FCSTD DOCUMENT  (FreeCAD 0.20R0.20)
Label: 009
License: All rights reserved
LicenseURL: http://en.wikipedia.org/wiki/All_rights_reserved
objects: Sketcher::SketchObject×1
note: 1 computed .brp shape members not serialized (recipe doc carries the construction recipe); baked Part::Feature solids carry a one-line shape summary decoded from their .brp

FEATURE [Sketcher::SketchObject] Sketch  label="baseL"
  FullyConstrained = false
  sketch-geometry (38):
    g0: LineSegment StartX=0 StartY=0 StartZ=0 EndX=0 EndY=200 EndZ=0
    g1: LineSegment StartX=390 StartY=200 StartZ=0 EndX=390 EndY=0 EndZ=0
    g2: LineSegment StartX=0 StartY=200 StartZ=0 EndX=190 EndY=200 EndZ=0
    g3: LineSegment StartX=0 StartY=0 StartZ=0 EndX=190 EndY=0 EndZ=0
    g4: LineSegment StartX=390 StartY=200 StartZ=0 EndX=200 EndY=200 EndZ=0
    g5: LineSegment StartX=390 StartY=0 StartZ=0 EndX=200 EndY=0 EndZ=0
    g6: LineSegment StartX=190 StartY=0 StartZ=0 EndX=190 EndY=14 EndZ=0
    g7: LineSegment StartX=200 StartY=0 StartZ=0 EndX=200 EndY=14 EndZ=0
    g8: LineSegment StartX=24 StartY=186 StartZ=0 EndX=190 EndY=105.929 EndZ=0
    g9: LineSegment StartX=16 StartY=178 StartZ=0 EndX=177.707 EndY=100 EndZ=0
    g10: LineSegment StartX=16 StartY=22 StartZ=0 EndX=177.707 EndY=100 EndZ=0
    g11: LineSegment StartX=24 StartY=14 StartZ=0 EndX=190 EndY=94.0706 EndZ=0
    g12: LineSegment StartX=16 StartY=22 StartZ=0 EndX=16 EndY=178 EndZ=0
    g13: LineSegment StartX=212.293 StartY=100 StartZ=0 EndX=374 EndY=22 EndZ=0
    g14: LineSegment StartX=200 StartY=94.0706 StartZ=0 EndX=366 EndY=14 EndZ=0
    g15: LineSegment StartX=374 StartY=178 StartZ=0 EndX=212.293 EndY=100 EndZ=0
    g16: LineSegment StartX=200 StartY=105.929 StartZ=0 EndX=366 EndY=186 EndZ=0
    g17: LineSegment StartX=212.293 StartY=100 StartZ=0 EndX=200 EndY=100 EndZ=0
    g18: LineSegment StartX=374 StartY=178 StartZ=0 EndX=374 EndY=22 EndZ=0
    g19: LineSegment StartX=366 StartY=14 StartZ=0 EndX=200 EndY=14 EndZ=0
    g20: LineSegment StartX=200 StartY=186 StartZ=0 EndX=366 EndY=186 EndZ=0
    g21: LineSegment StartX=24 StartY=14 StartZ=0 EndX=190 EndY=14 EndZ=0
    g22: LineSegment StartX=190 StartY=186 StartZ=0 EndX=24 EndY=186 EndZ=0
    g23: LineSegment StartX=177.707 StartY=100 StartZ=0 EndX=190 EndY=100 EndZ=0
    g24: Circle CenterX=190 CenterY=100 CenterZ=0 NormalX=0 NormalY=0 NormalZ=1 AngleXU=0 Radius=22.2927
    g25: Circle CenterX=190 CenterY=100 CenterZ=0 NormalX=0 NormalY=0 NormalZ=1 AngleXU=0 Radius=11.6257
    g26: LineSegment StartX=190 StartY=94.0706 StartZ=0 EndX=190.36 EndY=94.2444 EndZ=0
    g27: Circle CenterX=200 CenterY=100 CenterZ=0 NormalX=0 NormalY=0 NormalZ=1 AngleXU=0 Radius=11.2273
    g28: Circle CenterX=200 CenterY=100 CenterZ=0 NormalX=0 NormalY=0 NormalZ=1 AngleXU=0 Radius=22.2927
    g29: LineSegment StartX=190 StartY=200 StartZ=0 EndX=190 EndY=195.3 EndZ=0
    g30: LineSegment StartX=200 StartY=200 StartZ=0 EndX=200 EndY=195 EndZ=0
    g31: LineSegment StartX=190 StartY=195.3 StartZ=0 EndX=184 EndY=195.3 EndZ=0
    g32: LineSegment StartX=184 StartY=195.3 StartZ=0 EndX=184 EndY=193 EndZ=0
    g33: LineSegment StartX=184 StartY=193 StartZ=0 EndX=184 EndY=196.5 EndZ=0
    g34: Circle CenterX=184 CenterY=193 CenterZ=0 NormalX=0 NormalY=0 NormalZ=1 AngleXU=0 Radius=3.5
    g35: LineSegment StartX=190 StartY=186 StartZ=0 EndX=190 EndY=190.7 EndZ=0
    g36: LineSegment StartX=190 StartY=190.7 StartZ=0 EndX=184.163 EndY=190.7 EndZ=0
    g37: LineSegment StartX=200 StartY=186 StartZ=0 EndX=200 EndY=191 EndZ=0
  constraints (96):
    c: Coincident(g0,g-1)
    c: Vertical(g0)
    c: Distance(g0) = 200
    c: Vertical(g1)
    c: Distance(g1) = 200
    c: Coincident(g2,g0)
    c: Horizontal(g2)
    c: Distance(g2) = 190
    c: Coincident(g3,g0)
    c: Horizontal(g3)
    c: Distance(g3) = 190
    c: Block(g1)
    c: Coincident(g4,g1)
    c: Horizontal(g4)
    c: Coincident(g5,g1)
    c: Horizontal(g5)
    c: Distance(g5) = 190
    c: Distance(g4) = 190
    c: Coincident(g6,g3)
    c: Vertical(g6)
    c: Coincident(g7,g5)
    c: Vertical(g7)
    c: Distance(g6) = 14
    c: Distance(g7) = 14
    c: Block(g8)
    c: Block(g9)
    c: PointOnObject(g11,g9)
    c: Block(g11)
    c: Block(g10)
    c: Coincident(g10,g9)
    c: Vertical(g12)
    c: Block(g12)
    c: Block(g16)
    c: Block(g15)
    c: Block(g13)
    c: Block(g14)
    c: PointOnObject(g16,g13)
    c: PointOnObject(g14,g15)
    c: Coincident(g13,g15)
    c: Coincident(g17,g13)
    c: Horizontal(g17)
    c: Block(g17)
    c: Coincident(g18,g15)
    c: Coincident(g18,g13)
    c: Vertical(g18)
    c: Coincident(g19,g14)
    c: Coincident(g19,g7)
    c: Horizontal(g19)
    c: Coincident(g20,g16)
    c: Horizontal(g20)
    c: Coincident(g21,g11)
    c: Coincident(g21,g6)
    c: Horizontal(g21)
    c: Coincident(g22,g8)
    c: Horizontal(g22)
    c: Coincident(g23,g9)
    c: Horizontal(g23)
    c: Block(g23)
    c: Coincident(g24,g23)
    c: PointOnObject(g13,g24)
    c: Coincident(g25,g23)
    c: PointOnObject(g14,g25)
    c: Coincident(g26,g11)
    c: Angle(g11,g26) = 3.14159
    c: Distance(g26) = 0.4
    c: Coincident(g27,g17)
    c: PointOnObject(g26,g27)
    c: Coincident(g28,g17)
    c: PointOnObject(g9,g28)
    c: Block(g22)
    c: Coincident(g29,g2)
    c: Vertical(g29)
    c: Distance(g29) = 4.7
    c: Coincident(g30,g4)
    c: Vertical(g30)
    c: Block(g20)
    c: Distance(g30) = 5
    c: Coincident(g31,g29)
    c: Horizontal(g31)
    c: Distance(g31) = 6
    c: Coincident(g32,g31)
    c: Vertical(g32)
    c: Distance(g32) = 2.3
    c: Coincident(g33,g32)
    c: Vertical(g33)
    c: Distance(g33) = 3.5
    c: Coincident(g34,g32)
    c: PointOnObject(g33,g34)
    c: Coincident(g35,g22)
    c: Vertical(g35)
    c: Distance(g35) = 4.7
    c: Coincident(g36,g35)
    c: Horizontal(g36)
    c: Coincident(g37,g20)
    c: Vertical(g37)
    c: Distance(g37) = 5
